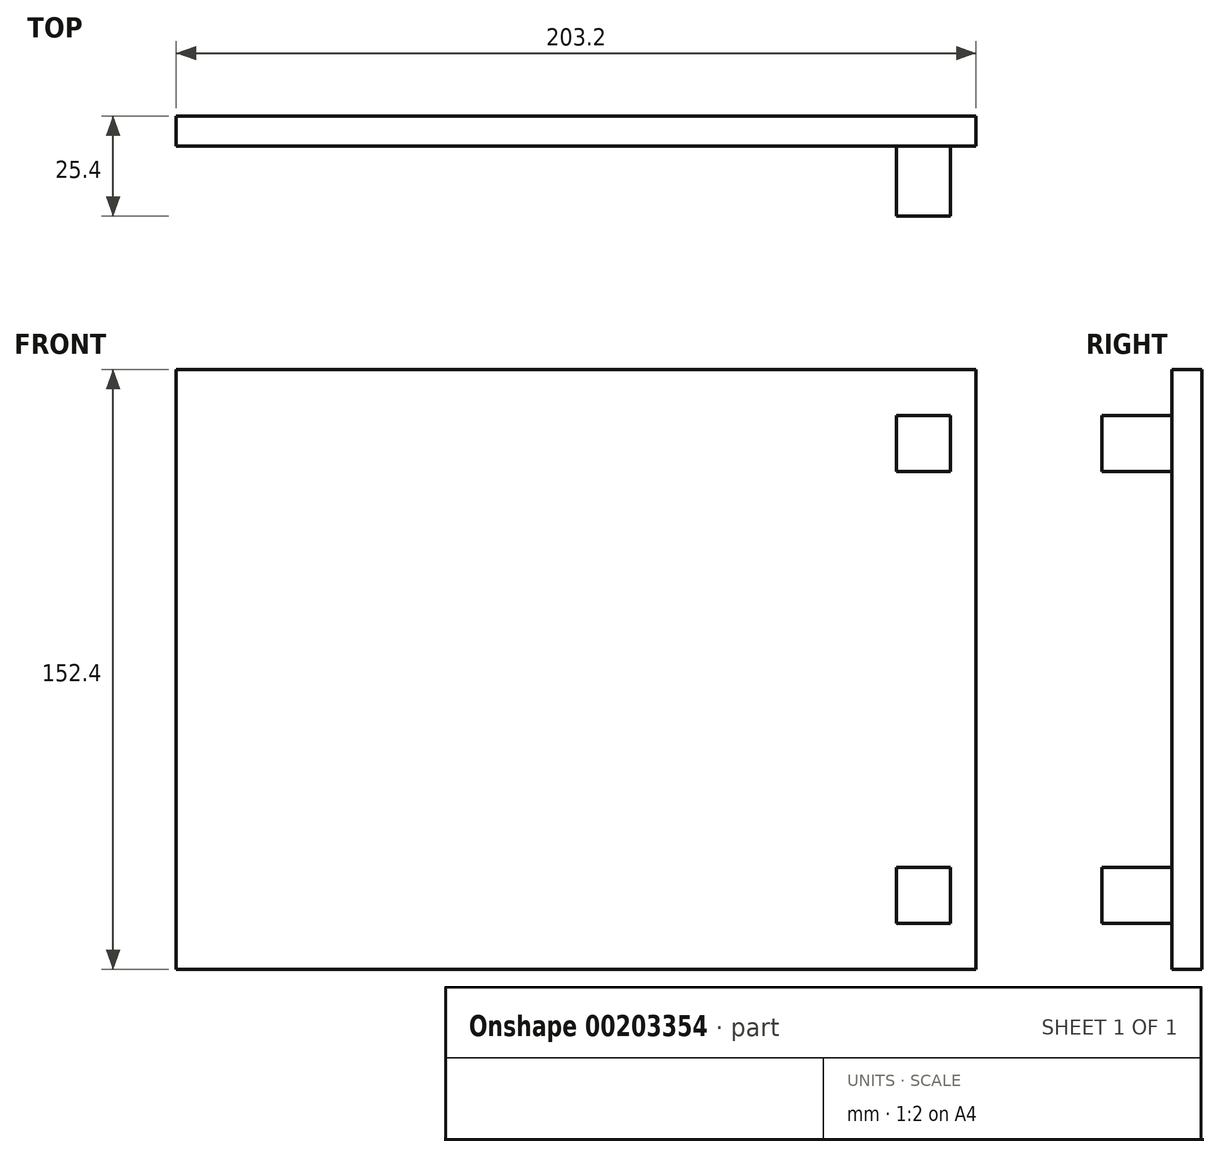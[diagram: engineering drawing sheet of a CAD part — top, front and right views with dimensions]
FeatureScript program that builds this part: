
annotation { "Feature Type Name" : "Feature", "Feature Type Description" : "" }
export const myFeature = defineFeature(function(context is Context, id is Id, definition is map)
    precondition{}
    {
        {
            var Q0;
            Q0=qCreatedBy(makeId("Front.planeOp"),FACE);
            var sketch = newSketch(context, id + "F0", { "sketchPlane" : qUnion([Q0])});
            skLineSegment(sketch, "E0.bottom", {"start": v(-101.6, 76.2) * mm, "end": v(101.6, 76.2) * mm});
            skLineSegment(sketch, "E0.top", {"start": v(-101.6, -76.2) * mm, "end": v(101.6, -76.2) * mm});
            skLineSegment(sketch, "E0.left", {"start": v(-101.6, 76.2) * mm, "end": v(-101.6, -76.2) * mm});
            skLineSegment(sketch, "E0.right", {"start": v(101.6, 76.2) * mm, "end": v(101.6, -76.2) * mm});
            skPoint(sketch, "E0.middle", {"position": v(0, 0) * mm});
            skSolve(sketch);
        }
        {
            var Q0;
            Q0 = qSketchRegion(id + "F0", true);
            extrude(context, id + "F1", {"entities" : qUnion([Q0]), "depth" : 7.62 * mm});
        }
        {
            var Q0;
            Q0=makeQuery(id+"F1.opExtrude","CAP_FACE",FACE,{"disambiguationData":[OSD([sQuery(id+"F0.wireOp",EDGE,"E0.bottom"),sQuery(id+"F0.wireOp",EDGE,"E0.top"),sQuery(id+"F0.wireOp",EDGE,"E0.left"),sQuery(id+"F0.wireOp",EDGE,"E0.right")])],"isStart":false});
            var sketch = newSketch(context, id + "F2", { "sketchPlane" : qUnion([Q0])});
            skLineSegment(sketch, "E1.bottom", {"start": v(81.39, -64.54) * mm, "end": v(95.15, -64.54) * mm});
            skLineSegment(sketch, "E1.top", {"start": v(81.39, -50.3) * mm, "end": v(95.15, -50.3) * mm});
            skLineSegment(sketch, "E1.left", {"start": v(81.39, -64.54) * mm, "end": v(81.39, -50.3) * mm});
            skLineSegment(sketch, "E1.right", {"start": v(95.15, -64.54) * mm, "end": v(95.15, -50.3) * mm});
            skLineSegment(sketch, "E2.MirrorCS", {"start": v(81.39, 64.54) * mm, "end": v(95.15, 64.54) * mm});
            skLineSegment(sketch, "E3.MirrorCS", {"start": v(95.15, 64.54) * mm, "end": v(95.15, 50.3) * mm});
            skLineSegment(sketch, "E4.MirrorCS", {"start": v(81.39, 64.54) * mm, "end": v(81.39, 50.3) * mm});
            skLineSegment(sketch, "E5.MirrorCS", {"start": v(81.39, 50.3) * mm, "end": v(95.15, 50.3) * mm});
            skSolve(sketch);
        }
        {
            var Q0;
            Q0=makeQuery(id+"F2.imprint","IMPRINT",FACE,{"disambiguationData":[TD([[makeQuery(id+"F2.imprint","IMPRINT",EDGE,{"derivedFrom":sQuery(id+"F2.wireOp",EDGE,"E2.MirrorCS")}),-1.0]])]});
            var Q1;
            Q1=makeQuery(id+"F2.imprint","IMPRINT",FACE,{"disambiguationData":[TD([[makeQuery(id+"F2.imprint","IMPRINT",EDGE,{"derivedFrom":sQuery(id+"F2.wireOp",EDGE,"E1.bottom")}),1.0]])]});
            extrude(context, id + "F3", {"entities" : qUnion([Q0, Q1]), "operationType" : NewBodyOperationType.ADD, "depth" : 17.78 * mm});
        }
    });
